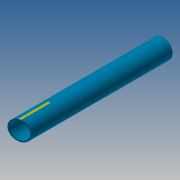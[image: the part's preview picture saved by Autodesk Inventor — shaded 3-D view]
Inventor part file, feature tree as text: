
AUTODESK INVENTOR PART (.ipt)
format: ipt  version: 2014 SP1 (Build 180222100, 222)  size: 133,120 bytes
history: native  units: in
note: dims shown in document units (in); Inventor stores cm internally (conversion verified against a paired STEP export)
features: sketch x7, extrude x4, plane x3, hole x1, other x1
ambient origin geometry x8: Origin, YZ Plane, XZ Plane, XY Plane, X Axis, Y Axis, Z Axis, Center Point
bodies: Solid1 (feature_tree)
feature tree (16):
  extrude  "Extrusion1"  Depth=0.154in
  sketch  "Sketch18"  dims[d3=17.7874in d4=0.0in d60=15.0deg]
  plane  "Work Plane9"
  extrude  "Extrusion11"  TaperAngle=15.0deg  [1 undecoded]
  sketch  "Sketch20"  dims[d64=0.3937in d65=3.937in]
  plane  "Work Plane10"
  plane  "Work Plane11"
  extrude  "flat1"  Depth=1.0in TaperAngle=0.0deg
  extrude  "flat2"  Depth=0.3937in
  hole  "Hole1"  [1 undecoded]
  sketch  "Sketch1"  dims[d0=2.375in d2=0.154in]
  other  "Work Axis2"
  sketch  "Sketch19"  dims[d61=4.0in d62=1.0in d63=0.0in]
  sketch  "Sketch21"  dims[d66=0.01in d67=0.0in d68=0.3937in]
  sketch  "Sketch22"  dims[d69=3.937in]
  sketch  "Sketch23"  dims[d70=0.01in d71=0.0in d73=1.5748in d74=0.7874in d75=0.125in d76=0.75in d77=0.375in d78=0.25in d79=0.5635in d80=1.0in d81=0.8108in d82=13.8504in d83=13.8504in]
note: 2 required parameter values undecoded (feature->parameter linkage not recoverable at this tier; creation-order binding heuristic only, values carry confidence <= 0.55)
